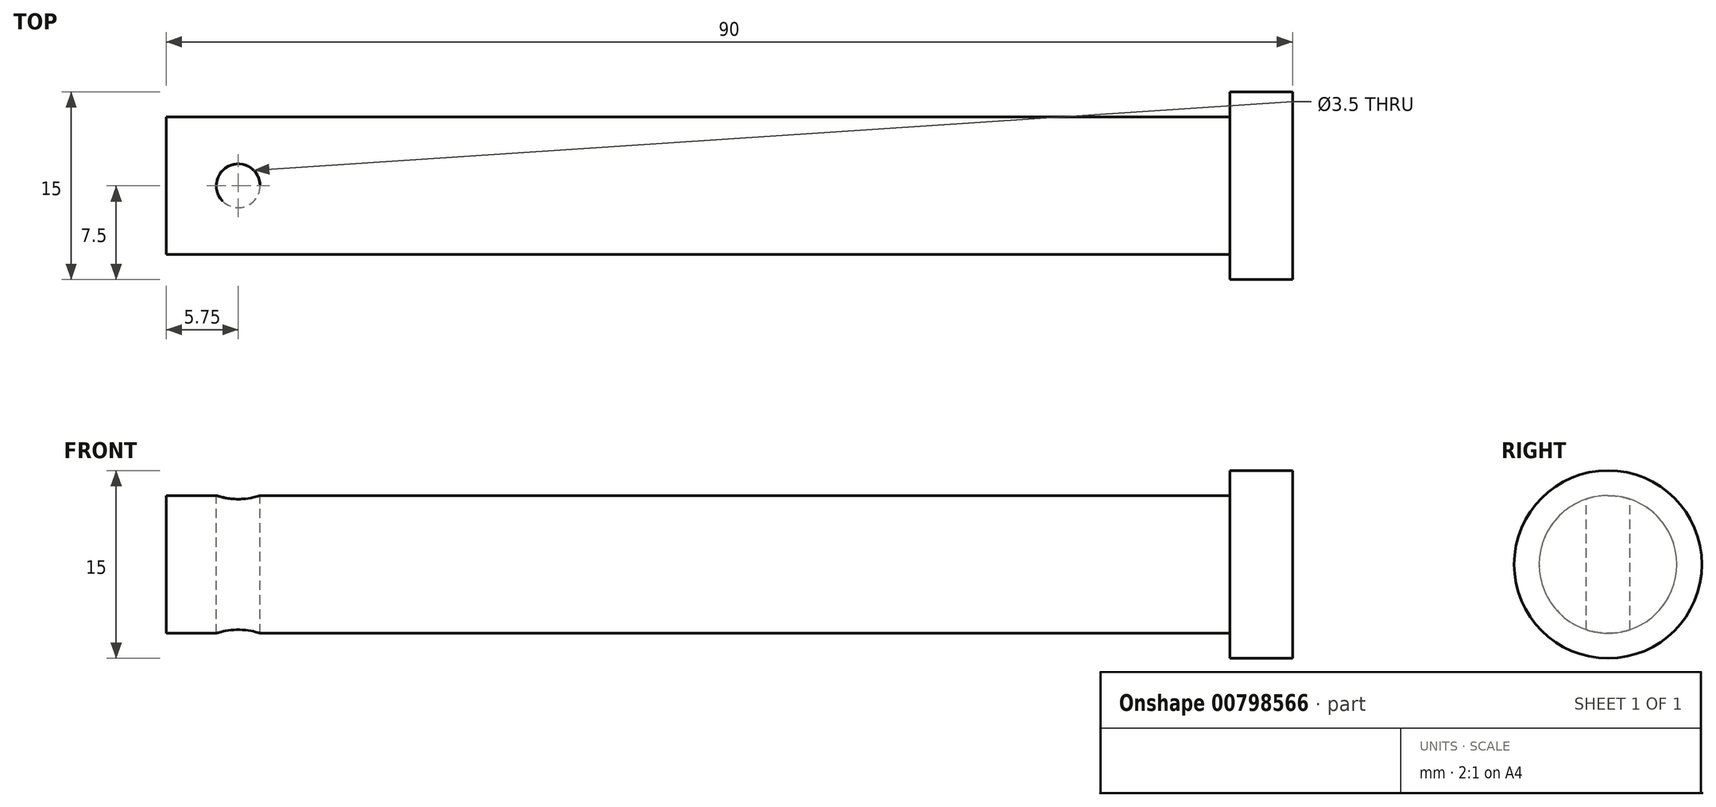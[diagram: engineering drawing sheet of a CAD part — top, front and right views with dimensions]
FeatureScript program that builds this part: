
annotation { "Feature Type Name" : "Feature", "Feature Type Description" : "" }
export const myFeature = defineFeature(function(context is Context, id is Id, definition is map)
    precondition{}
    {
        {
            var Q0;
            Q0=qCreatedBy(makeId("Front.planeOp"),FACE);
            var sketch = newSketch(context, id + "F0", { "sketchPlane" : qUnion([Q0])});
            skLineSegment(sketch, "E0", {"start": v(-45, 0) * mm, "end": v(45, 0) * mm});
            skLineSegment(sketch, "E1", {"start": v(45, 0) * mm, "end": v(45, 5.5) * mm});
            skLineSegment(sketch, "E2", {"start": v(45, 5.5) * mm, "end": v(-45, 5.5) * mm});
            skLineSegment(sketch, "E3", {"start": v(-45, 5.5) * mm, "end": v(-45, 0) * mm});
            skSolve(sketch);
        }
        {
            var Q0;
            Q0 = qSketchRegion(id + "F0", true);
            var Q1;
            Q1=sQuery(id+"F0.wireOp",EDGE,"E0");
            revolve(context, id + "F1", {"surfaceOperationType" : NewSurfaceOperationType.NEW, "entities" : qUnion([Q0]), "axis" : qUnion([Q1]), "revolveType" : RevolveType.FULL});
        }
        {
            var Q0;
            Q0=qCreatedBy(makeId("Top.planeOp"),FACE);
            var sketch = newSketch(context, id + "F2", { "sketchPlane" : qUnion([Q0])});
            skPoint(sketch, "E4", {"position": v(-39.25, 0) * mm});
            skCircle(sketch, "E5", {"center": v(-39.25, 0) * mm, "radius": 1.75 * mm});
            skSolve(sketch);
        }
        {
            var Q0;
            Q0 = qSketchRegion(id + "F2", true);
            extrude(context, id + "F3", {"entities" : qUnion([Q0]), "operationType" : NewBodyOperationType.REMOVE, "oppositeDirection" : true, "depth" : 30 * mm, "offsetDistance" : 25 * mm, "symmetric" : true});
        }
        {
            var Q0;
            Q0=makeQuery(id+"F1.opRevolve","SWEPT_FACE",FACE,{"disambiguationData":[OSD([sQuery(id+"F0.wireOp",EDGE,"E1")])]});
            var sketch = newSketch(context, id + "F4", { "sketchPlane" : qUnion([Q0])});
            skCircle(sketch, "E6", {"center": v(0, 0) * mm, "radius": 7.5 * mm});
            skSolve(sketch);
        }
        {
            var Q0;
            Q0=makeQuery(id+"F4.imprint","IMPRINT",FACE,{"disambiguationData":[TD([[makeQuery(id+"F4.imprint","IMPRINT",EDGE,{"derivedFrom":sQuery(id+"F4.wireOp",EDGE,"E6")}),1.0]])]});
            extrude(context, id + "F5", {"entities" : qUnion([Q0]), "operationType" : NewBodyOperationType.ADD, "oppositeDirection" : true, "depth" : 5 * mm, "offsetDistance" : 25 * mm});
        }
    });
